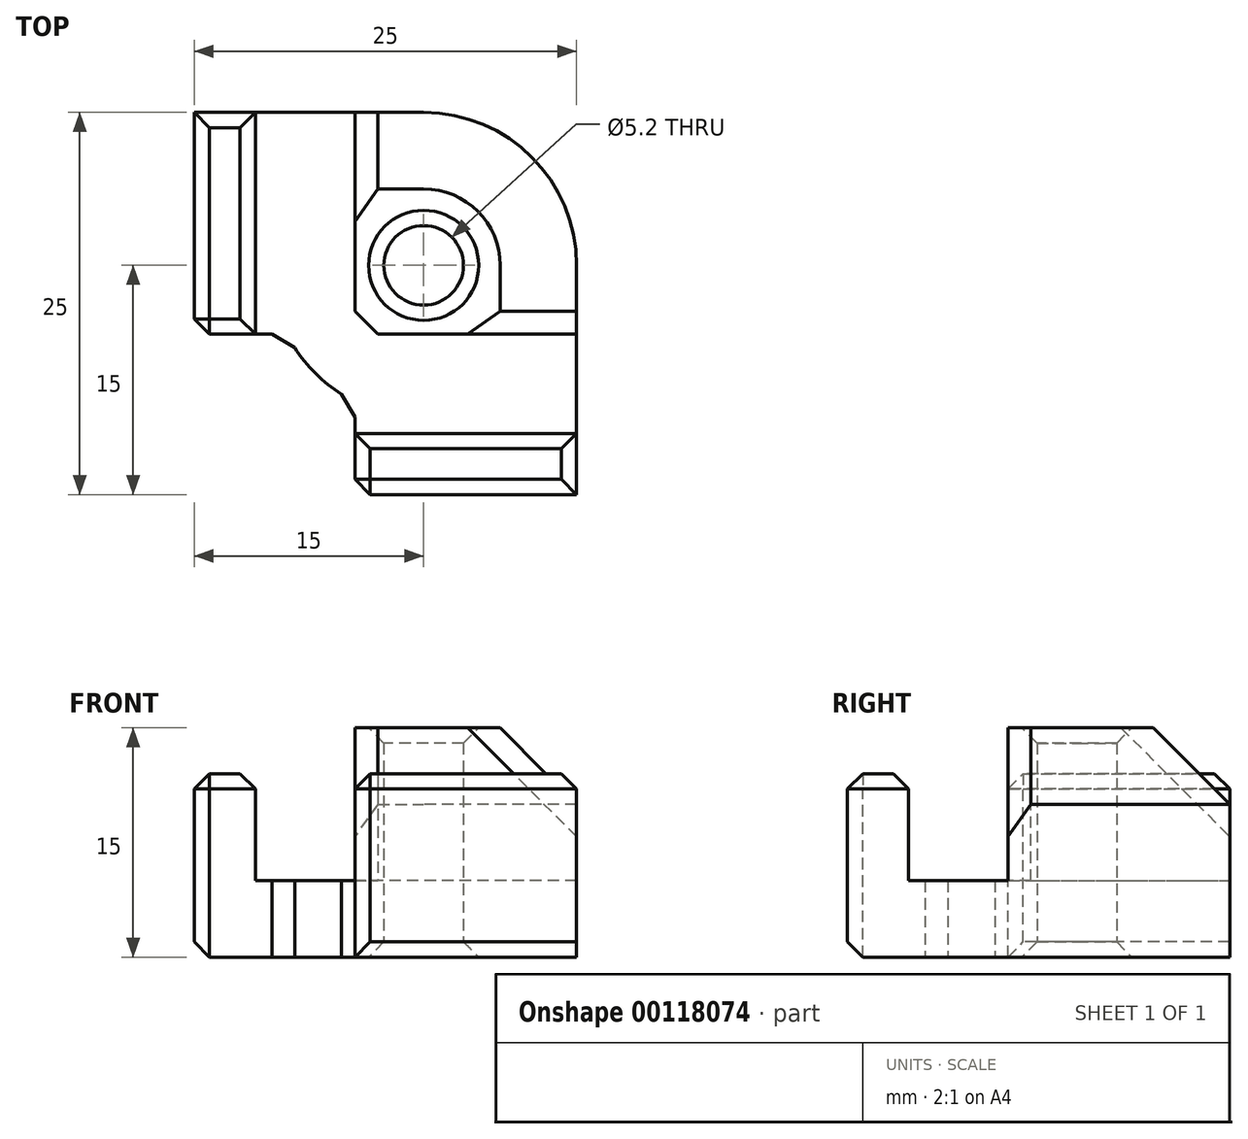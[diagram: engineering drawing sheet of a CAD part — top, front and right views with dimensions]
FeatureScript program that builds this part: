
annotation { "Feature Type Name" : "Feature", "Feature Type Description" : "" }
export const myFeature = defineFeature(function(context is Context, id is Id, definition is map)
    precondition{}
    {
        {
            var Q0;
            Q0=qCreatedBy(makeId("Top.planeOp"),FACE);
            var sketch = newSketch(context, id + "F0", { "sketchPlane" : qUnion([Q0])});
            skCircle(sketch, "E0", {"center": v(0, 0) * mm, "radius": 2.6 * mm});
            skArc(sketch, "E1", {"start": v(-8.93, -4.5) * mm, "mid": v(-7.07, -7.07) * mm, "end": v(-4.5, -8.93) * mm});
            skLineSegment(sketch, "E2.bottom", {"start": v(-11, -4.5) * mm, "end": v(10, -4.5) * mm});
            skLineSegment(sketch, "E2.right", {"start": v(10, -4.5) * mm, "end": v(10, -11) * mm});
            skLineSegment(sketch, "E3.bottom", {"start": v(-11, 10) * mm, "end": v(-4.5, 10) * mm});
            skLineSegment(sketch, "E3.left", {"start": v(-11, 10) * mm, "end": v(-11, -4.5) * mm});
            skLineSegment(sketch, "E3.right", {"start": v(-4.5, 10) * mm, "end": v(-4.5, -11) * mm});
            skLineSegment(sketch, "E4.trimOffspring", {"start": v(-4.5, -11) * mm, "end": v(10, -11) * mm});
            skLineSegment(sketch, "E5", {"start": v(-11, 10) * mm, "end": v(-15, 10) * mm});
            skLineSegment(sketch, "E6", {"start": v(-15, 10) * mm, "end": v(-15, -4.5) * mm});
            skLineSegment(sketch, "E7", {"start": v(-15, -4.5) * mm, "end": v(-11, -4.5) * mm});
            skLineSegment(sketch, "E8", {"start": v(-4.5, -11) * mm, "end": v(-4.5, -15) * mm});
            skLineSegment(sketch, "E9", {"start": v(-4.5, -15) * mm, "end": v(10, -15) * mm});
            skLineSegment(sketch, "E10", {"start": v(10, -15) * mm, "end": v(10, -11) * mm});
            skLineSegment(sketch, "E11", {"start": v(-4.5, 10) * mm, "end": v(0, 10) * mm});
            skLineSegment(sketch, "E12", {"start": v(10, -4.5) * mm, "end": v(10, 0) * mm});
            skArc(sketch, "E13.trimOffspring", {"start": v(10, 0) * mm, "mid": v(7.07, 7.07) * mm, "end": v(0, 10) * mm});
            skSolve(sketch);
        }
        {
            var Q0;
            {var subQ0=sQuery(id+"F0.wireOp",EDGE,"E1");Q0=makeQuery(id+"F0.imprint","IMPRINT",FACE,{"disambiguationData":[TD([[makeQuery(id+"F0.imprint","IMPRINT",EDGE,{"derivedFrom":subQ0}),1.0]])]});}
            var Q1;
            {var subQ1=sQuery(id+"F0.wireOp",EDGE,"E3.bottom");Q1=makeQuery(id+"F0.imprint","IMPRINT",FACE,{"disambiguationData":[TD([[makeQuery(id+"F0.imprint","IMPRINT",EDGE,{"derivedFrom":subQ1}),-1.0]])]});}
            var Q2;
            Q2=makeQuery(id+"F0.imprint","IMPRINT",FACE,{"disambiguationData":[TD([[makeQuery(id+"F0.imprint","IMPRINT",EDGE,{"derivedFrom":sQuery(id+"F0.wireOp",EDGE,"E3.left")}),-1.0]])]});
            var Q3;
            Q3=makeQuery(id+"F0.imprint","IMPRINT",FACE,{"disambiguationData":[TD([[makeQuery(id+"F0.imprint","IMPRINT",EDGE,{"derivedFrom":sQuery(id+"F0.wireOp",EDGE,"E0")}),-1.0]])]});
            var Q4;
            {var subQ5=sQuery(id+"F0.wireOp",EDGE,"E2.right");Q4=makeQuery(id+"F0.imprint","IMPRINT",FACE,{"disambiguationData":[TD([[makeQuery(id+"F0.imprint","IMPRINT",EDGE,{"derivedFrom":subQ5}),-1.0]])]});}
            var Q5;
            Q5=makeQuery(id+"F0.imprint","IMPRINT",FACE,{"disambiguationData":[TD([[makeQuery(id+"F0.imprint","IMPRINT",EDGE,{"derivedFrom":sQuery(id+"F0.wireOp",EDGE,"E4.trimOffspring")}),-1.0]])]});
            extrude(context, id + "F1", {"entities" : qUnion([Q0, Q1, Q2, Q3, Q4, Q5]), "depth" : 5 * mm});
        }
        {
            var Q0;
            Q0=makeQuery(id+"F0.imprint","IMPRINT",FACE,{"disambiguationData":[TD([[makeQuery(id+"F0.imprint","IMPRINT",EDGE,{"derivedFrom":sQuery(id+"F0.wireOp",EDGE,"E3.left")}),-1.0]])]});
            var Q1;
            Q1=makeQuery(id+"F0.imprint","IMPRINT",FACE,{"disambiguationData":[TD([[makeQuery(id+"F0.imprint","IMPRINT",EDGE,{"derivedFrom":sQuery(id+"F0.wireOp",EDGE,"E4.trimOffspring")}),-1.0]])]});
            extrude(context, id + "F2", {"entities" : qUnion([Q0, Q1]), "operationType" : NewBodyOperationType.ADD, "depth" : 12 * mm});
        }
        {
            var Q0;
            Q0=makeQuery(id+"F0.imprint","IMPRINT",FACE,{"disambiguationData":[TD([[makeQuery(id+"F0.imprint","IMPRINT",EDGE,{"derivedFrom":sQuery(id+"F0.wireOp",EDGE,"E0")}),-1.0]])]});
            extrude(context, id + "F3", {"entities" : qUnion([Q0]), "operationType" : NewBodyOperationType.ADD, "depth" : 15 * mm});
        }
        {
            var Q0;
            Q0=makeQuery(id+"F3.opExtrude","SWEPT_EDGE",EDGE,{"disambiguationData":[OSD([sQuery(id+"F0.wireOp",EDGE,"E2.bottom"),sQuery(id+"F0.wireOp",EDGE,"E3.right")])]});
            chamfer(context, id + "F4", {"entities" : qUnion([Q0]), "width" : 1.5 * mm, "tangentPropagation" : true});
        }
        {
            var Q0;
            Q0=makeQuery(id+"F3.opExtrude","CAP_EDGE",EDGE,{"disambiguationData":[OSD([sQuery(id+"F0.wireOp",EDGE,"E13.trimOffspring")])],"isStart":false});
            chamfer(context, id + "F5", {"entities" : qUnion([Q0]), "width" : 5 * mm, "tangentPropagation" : true});
        }
        {
            var Q0;
            Q0=makeQuery(id+"F5.opChamfer","BLEND_EDGE",EDGE,{"blendedFrom":[makeQuery(id+"F3.opExtrude","CAP_EDGE",EDGE,{"disambiguationData":[OSD([sQuery(id+"F0.wireOp",EDGE,"E11")])],"isStart":false}),makeQuery(id+"F3.opExtrude","SWEPT_FACE",FACE,{"disambiguationData":[OSD([sQuery(id+"F0.wireOp",EDGE,"E3.right")])]})],"blendedInto":[makeQuery(id+"F3.opExtrude","SWEPT_FACE",FACE,{"disambiguationData":[OSD([sQuery(id+"F0.wireOp",EDGE,"E3.right")])]})]});
            var Q1;
            Q1=makeQuery(id+"F5.opChamfer","BLEND_EDGE",EDGE,{"blendedFrom":[makeQuery(id+"F3.opExtrude","CAP_EDGE",EDGE,{"disambiguationData":[OSD([sQuery(id+"F0.wireOp",EDGE,"E12")])],"isStart":false}),makeQuery(id+"F3.opExtrude","SWEPT_FACE",FACE,{"disambiguationData":[OSD([sQuery(id+"F0.wireOp",EDGE,"E2.bottom")])]})],"blendedInto":[makeQuery(id+"F3.opExtrude","SWEPT_FACE",FACE,{"disambiguationData":[OSD([sQuery(id+"F0.wireOp",EDGE,"E2.bottom")])]})]});
            chamfer(context, id + "F6", {"entities" : qUnion([Q0, Q1]), "width" : 1.5 * mm, "tangentPropagation" : true});
        }
        {
            var Q0;
            Q0=makeQuery(id+"F3.opExtrude","CAP_EDGE",EDGE,{"disambiguationData":[OSD([sQuery(id+"F0.wireOp",EDGE,"E0")])],"isStart":false});
            var Q1;
            Q1=makeQuery(id+"F1.opExtrude","CAP_EDGE",EDGE,{"disambiguationData":[OSD([sQuery(id+"F0.wireOp",EDGE,"E0")])],"isStart":true});
            var Q2;
            Q2=makeQuery(id+"F1.opExtrude","CAP_EDGE",EDGE,{"disambiguationData":[OSD([sQuery(id+"F0.wireOp",EDGE,"E6")])],"isStart":true});
            var Q3;
            Q3=makeQuery(id+"F1.opExtrude","CAP_EDGE",EDGE,{"disambiguationData":[OSD([sQuery(id+"F0.wireOp",EDGE,"E9")])],"isStart":true});
            var Q4;
            Q4=makeQuery(id+"F2.opExtrude","CAP_EDGE",EDGE,{"disambiguationData":[OSD([sQuery(id+"F0.wireOp",EDGE,"E9")])],"isStart":false});
            var Q5;
            Q5=makeQuery(id+"F2.opExtrude","CAP_EDGE",EDGE,{"disambiguationData":[OSD([sQuery(id+"F0.wireOp",EDGE,"E6")])],"isStart":false});
            var Q6;
            Q6=makeQuery(id+"F2.opExtrude","CAP_EDGE",EDGE,{"disambiguationData":[OSD([sQuery(id+"F0.wireOp",EDGE,"E7")])],"isStart":false});
            var Q7;
            Q7=makeQuery(id+"F2.opExtrude","CAP_EDGE",EDGE,{"disambiguationData":[OSD([sQuery(id+"F0.wireOp",EDGE,"E8")])],"isStart":false});
            var Q8;
            Q8=makeQuery(id+"F2.opExtrude","CAP_EDGE",EDGE,{"disambiguationData":[OSD([sQuery(id+"F0.wireOp",EDGE,"E10")])],"isStart":false});
            var Q9;
            Q9=makeQuery(id+"F2.opExtrude","CAP_EDGE",EDGE,{"disambiguationData":[OSD([sQuery(id+"F0.wireOp",EDGE,"E5")])],"isStart":false});
            var Q10;
            Q10=makeQuery(id+"F2.opExtrude","CAP_EDGE",EDGE,{"disambiguationData":[OSD([sQuery(id+"F0.wireOp",EDGE,"E4.trimOffspring")])],"isStart":false});
            var Q11;
            Q11=makeQuery(id+"F2.opExtrude","CAP_EDGE",EDGE,{"disambiguationData":[OSD([sQuery(id+"F0.wireOp",EDGE,"E3.left")])],"isStart":false});
            var Q12;
            {var subQ0=sQuery(id+"F0.wireOp",EDGE,"E9");var subQ1=sQuery(id+"F0.wireOp",EDGE,"E8");Q12=makeQuery(id+"F2.boolean.opBoolean","MERGE",EDGE,{"derivedFrom":[makeQuery(id+"F1.opExtrude","SWEPT_EDGE",EDGE,{"disambiguationData":[OSD([subQ1,subQ0])]}),makeQuery(id+"F2.opExtrude","SWEPT_EDGE",EDGE,{"disambiguationData":[OSD([subQ1,subQ0])]})]});}
            var Q13;
            {var subQ0=sQuery(id+"F0.wireOp",EDGE,"E7");var subQ1=sQuery(id+"F0.wireOp",EDGE,"E6");Q13=makeQuery(id+"F2.boolean.opBoolean","MERGE",EDGE,{"derivedFrom":[makeQuery(id+"F1.opExtrude","SWEPT_EDGE",EDGE,{"disambiguationData":[OSD([subQ1,subQ0])]}),makeQuery(id+"F2.opExtrude","SWEPT_EDGE",EDGE,{"disambiguationData":[OSD([subQ1,subQ0])]})]});}
            var Q14;
            Q14=makeQuery(id+"F1.opExtrude","SWEPT_EDGE",EDGE,{"disambiguationData":[OSD([sQuery(id+"F0.wireOp",EDGE,"E1"),sQuery(id+"F0.wireOp",EDGE,"E3.right")])]});
            var Q15;
            Q15=makeQuery(id+"F1.opExtrude","SWEPT_EDGE",EDGE,{"disambiguationData":[OSD([sQuery(id+"F0.wireOp",EDGE,"E1"),sQuery(id+"F0.wireOp",EDGE,"E2.bottom")])]});
            chamfer(context, id + "F7", {"entities" : qUnion([Q0, Q1, Q2, Q3, Q4, Q5, Q6, Q7, Q8, Q9, Q10, Q11, Q12, Q13, Q14, Q15]), "width" : 1 * mm, "tangentPropagation" : true});
        }
    });
